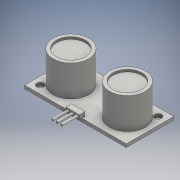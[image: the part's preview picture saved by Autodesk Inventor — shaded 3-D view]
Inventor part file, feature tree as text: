
AUTODESK INVENTOR PART (.ipt)
format: ipt  version: 2016 (Build 200138000, 138)  size: 166,912 bytes
history: native  units: mm
features: extrude x5, sketch x5, other x1
ambient origin geometry x8: Origin, YZ Plane, XZ Plane, XY Plane, X Axis, Y Axis, Z Axis, Center Point
bodies: Body1 (feature_tree)
feature tree (11):
  other  "ソリッド1"
  extrude  "押し出し1"  Depth=45.7mm
  extrude  "押し出し2"  Depth=21.3mm
  extrude  "押し出し3"  Depth=3.5mm
  extrude  "押し出し4"  Depth=3.5mm
  extrude  "押し出し5"  Depth=3.5mm
  sketch  "スケッチ1"
  sketch  "スケッチ2"
  sketch  "スケッチ3"
  sketch  "スケッチ4"
  sketch  "スケッチ5"
